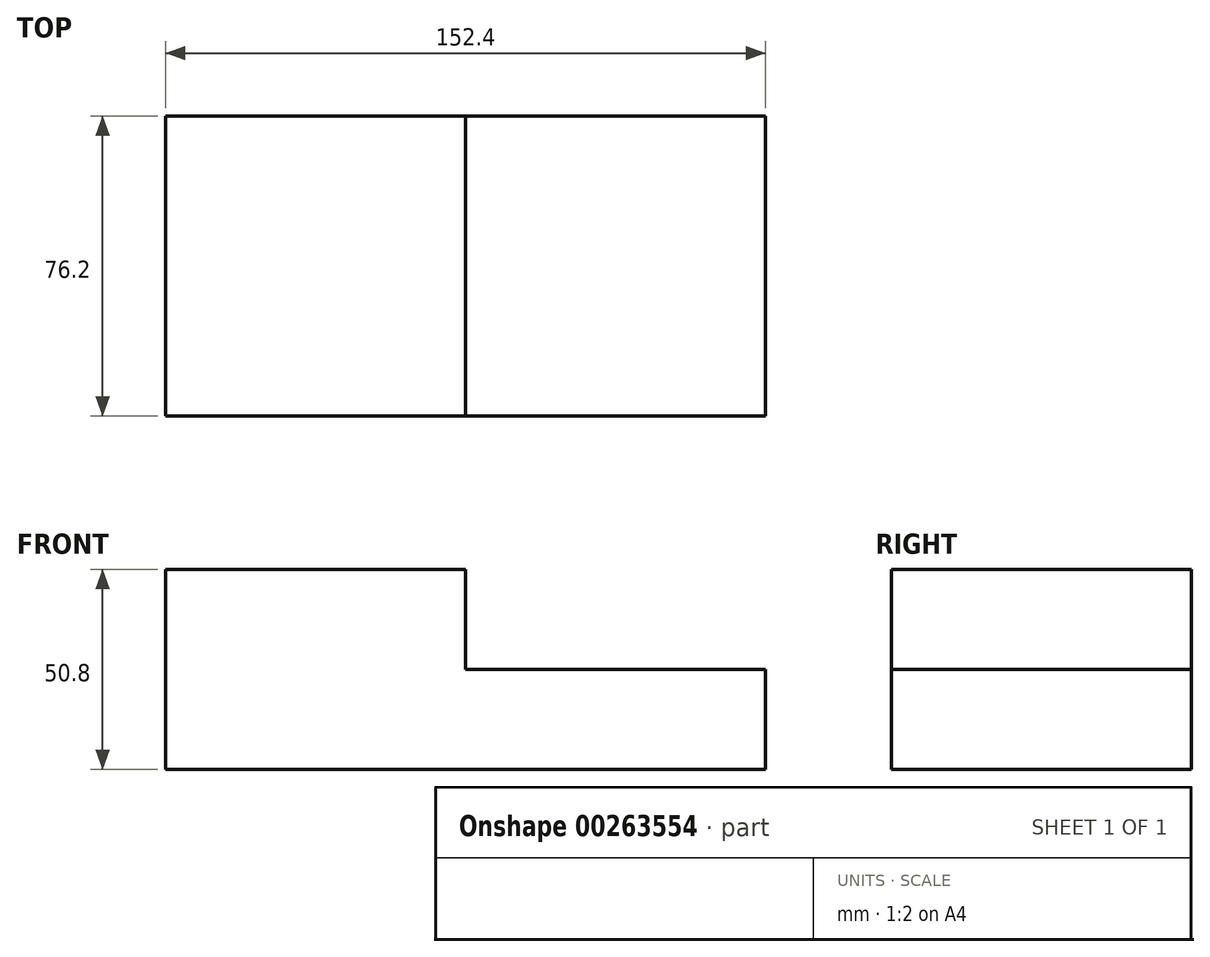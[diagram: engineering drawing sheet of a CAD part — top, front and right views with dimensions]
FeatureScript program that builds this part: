
annotation { "Feature Type Name" : "Feature", "Feature Type Description" : "" }
export const myFeature = defineFeature(function(context is Context, id is Id, definition is map)
    precondition{}
    {
        {
            var Q0;
            Q0=qCreatedBy(makeId("Front.planeOp"),FACE);
            var sketch = newSketch(context, id + "F0", { "sketchPlane" : qUnion([Q0])});
            skLineSegment(sketch, "E0", {"start": v(-76.2, 16.64) * mm, "end": v(-76.2, -34.16) * mm});
            skLineSegment(sketch, "E1", {"start": v(-76.2, -34.16) * mm, "end": v(76.2, -34.16) * mm});
            skLineSegment(sketch, "E2", {"start": v(76.2, -34.16) * mm, "end": v(76.2, -8.76) * mm});
            skLineSegment(sketch, "E3", {"start": v(76.2, -8.76) * mm, "end": v(0, -8.76) * mm});
            skLineSegment(sketch, "E4", {"start": v(0, -8.76) * mm, "end": v(0, 16.64) * mm});
            skLineSegment(sketch, "E5", {"start": v(0, 16.64) * mm, "end": v(-76.2, 16.64) * mm});
            skSolve(sketch);
        }
        {
            var Q0;
            Q0=makeQuery(id+"F0.imprint","IMPRINT",FACE,{"disambiguationData":[TD([[makeQuery(id+"F0.imprint","IMPRINT",EDGE,{"derivedFrom":sQuery(id+"F0.wireOp",EDGE,"E0")}),1.0]])]});
            extrude(context, id + "F1", {"entities" : qUnion([Q0]), "depth" : 76.2 * mm});
        }
    });
